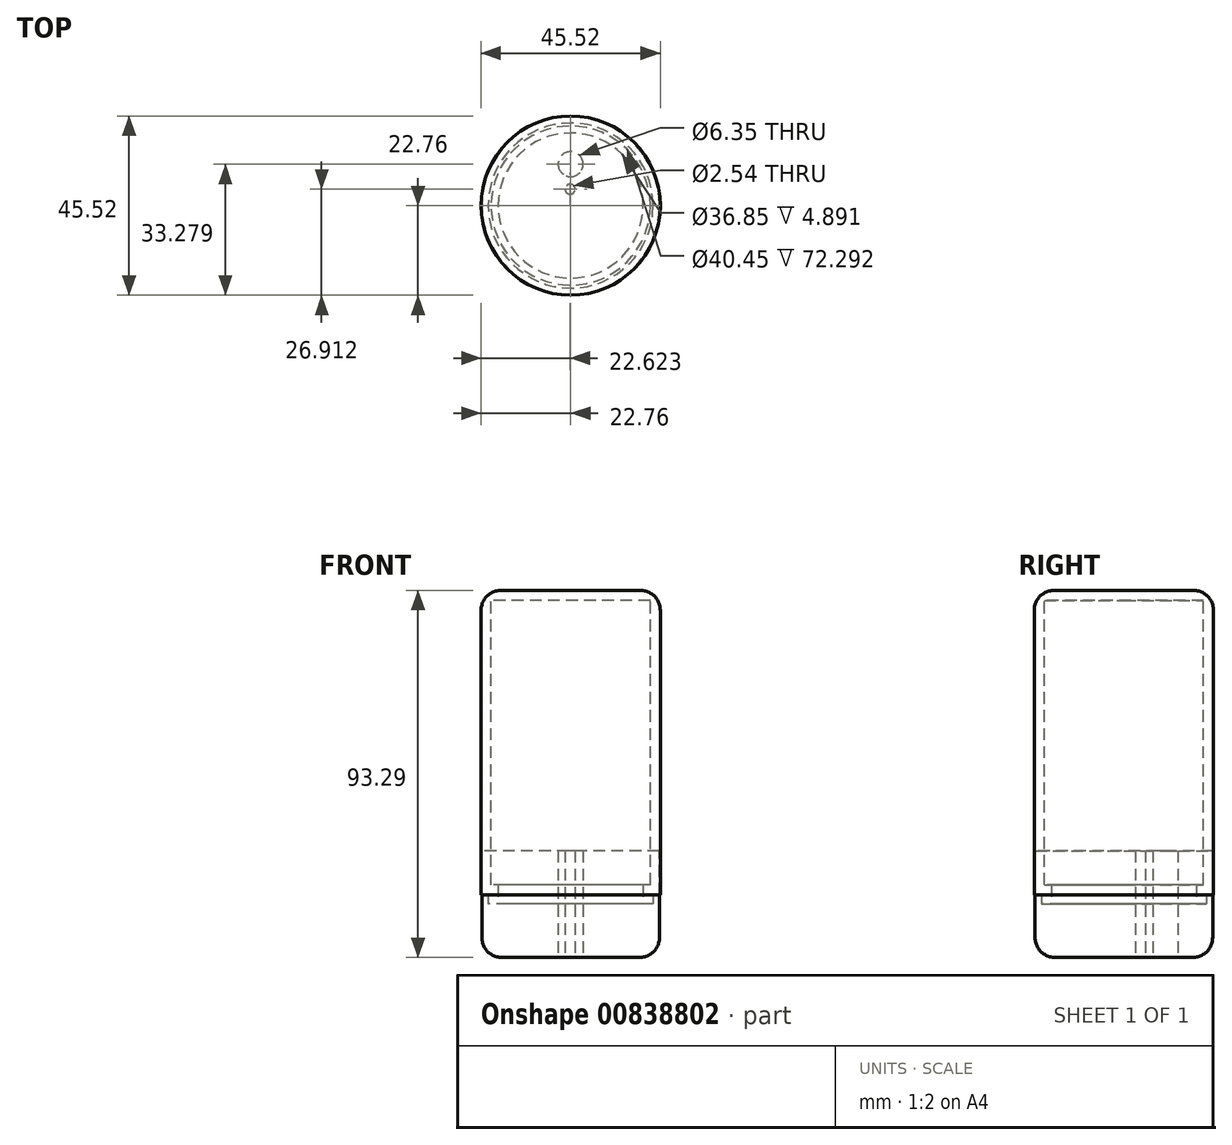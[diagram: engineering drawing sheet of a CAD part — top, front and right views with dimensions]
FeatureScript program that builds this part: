
annotation { "Feature Type Name" : "Feature", "Feature Type Description" : "" }
export const myFeature = defineFeature(function(context is Context, id is Id, definition is map)
    precondition{}
    {
        {
            var Q0;
            Q0=qCreatedBy(makeId("Top.planeOp"),FACE);
            var sketch = newSketch(context, id + "F0", { "sketchPlane" : qUnion([Q0])});
            skCircle(sketch, "E0", {"center": v(0, 0) * mm, "radius": 20.96 * mm});
            skSolve(sketch);
        }
        {
            var Q0;
            Q0=makeQuery(id+"F0.imprint","IMPRINT",FACE,{"disambiguationData":[TD([[makeQuery(id+"F0.imprint","IMPRINT",EDGE,{"derivedFrom":sQuery(id+"F0.wireOp",EDGE,"E0")}),1.0]])]});
            var Q1;
            Q1=sQuery(id+"F0.wireOp",EDGE,"E0");
            extrude(context, id + "F1", {"entities" : qUnion([Q0]), "surfaceEntities" : qUnion([Q1]), "depth" : 79.72 * mm, "offsetDistance" : 25.4 * mm});
        }
        {
            var Q0;
            Q0=makeQuery(id+"F1.opExtrude","CAP_FACE",FACE,{"disambiguationData":[OSD([sQuery(id+"F0.wireOp",EDGE,"E0")])],"isStart":false});
            var sketch = newSketch(context, id + "F2", { "sketchPlane" : qUnion([Q0])});
            skCircle(sketch, "E1", {"center": v(0, 0) * mm, "radius": 22.76 * mm});
            skSolve(sketch);
        }
        {
            var Q0;
            Q0=makeQuery(id+"F2.imprint","IMPRINT",FACE,{"disambiguationData":[TD([[makeQuery(id+"F2.imprint","IMPRINT",EDGE,{"derivedFrom":sQuery(id+"F2.wireOp",EDGE,"E1")}),1.0]])]});
            var Q1;
            Q1=sQuery(id+"F2.wireOp",EDGE,"E1");
            extrude(context, id + "F3", {"entities" : qUnion([Q0]), "operationType" : NewBodyOperationType.ADD, "surfaceEntities" : qUnion([Q1]), "oppositeDirection" : true, "depth" : 77.37 * mm, "offsetDistance" : 25.4 * mm});
        }
        {
            var Q0;
            Q0=makeQuery(id+"F1.opExtrude","CAP_FACE",FACE,{"disambiguationData":[OSD([sQuery(id+"F0.wireOp",EDGE,"E0")])],"isStart":true});
            shell(context, id + "F4", {"entities" : qUnion([Q0]), "thickness" : 2.54 * mm});
        }
        {
            var Q0;
            Q0=makeQuery(id+"F3.opExtrude","CAP_EDGE",EDGE,{"disambiguationData":[OSD([sQuery(id+"F2.wireOp",EDGE,"E1")])],"isStart":true});
            fillet(context, id + "F5", {"entities" : qUnion([Q0]), "radius" : 5.08 * mm, "tangentPropagation" : true, "allowEdgeOverflow" : false});
        }
        {
            var Q0;
            Q0=qCreatedBy(makeId("Top.planeOp"),FACE);
            var sketch = newSketch(context, id + "F6", { "sketchPlane" : qUnion([Q0])});
            skCircle(sketch, "E2", {"center": v(0, 0) * mm, "radius": 22.56 * mm});
            skSolve(sketch);
        }
        {
            var Q0;
            Q0=makeQuery(id+"F6.imprint","IMPRINT",FACE,{"disambiguationData":[TD([[makeQuery(id+"F6.imprint","IMPRINT",EDGE,{"derivedFrom":sQuery(id+"F6.wireOp",EDGE,"E2")}),1.0]])]});
            var Q1;
            Q1=sQuery(id+"F6.wireOp",EDGE,"E2");
            extrude(context, id + "F7", {"entities" : qUnion([Q0]), "surfaceEntities" : qUnion([Q1]), "endBound" : BoundingType.SYMMETRIC, "oppositeDirection" : true, "depth" : 27.14 * mm, "offsetDistance" : 25.4 * mm});
        }
        {
            var Q0;
            Q0=makeQuery(id+"F7.opExtrude","CAP_FACE",FACE,{"disambiguationData":[OSD([sQuery(id+"F6.wireOp",EDGE,"E2")])],"isStart":false});
            var sketch = newSketch(context, id + "F8", { "sketchPlane" : qUnion([Q0])});
            skPoint(sketch, "E3", {"position": v(0, -10.52) * mm});
            skSolve(sketch);
        }
        {
            var Q0;
            Q0=sQuery(id+"F8.wireOp",VERTEX,"E3");
            var Q1;
            Q1=makeQuery(id+"F7.opExtrude","SWEPT_BODY",BODY,{"disambiguationData":[OSD([sQuery(id+"F6.wireOp",EDGE,"E2")])]});
            hole(context, id + "F9", {"style" : HoleStyle.SIMPLE, "endStyle" : HoleEndStyle.BLIND, "holeDiameter" : 6.35 * mm, "majorDiameter" : 6.35 * mm, "holeDepth" : 31.75 * mm, "isTappedThrough" : true, "tappedDepth" : 12.7 * mm, "tapClearance" : 3, "locations" : qUnion([Q0]), "scope" : qUnion([Q1])});
        }
        {
            var Q0;
            Q0=makeQuery(id+"F7.opExtrude","CAP_EDGE",EDGE,{"disambiguationData":[OSD([sQuery(id+"F6.wireOp",EDGE,"E2")])],"isStart":false});
            fillet(context, id + "F10", {"entities" : qUnion([Q0]), "radius" : 5.08 * mm, "tangentPropagation" : true, "allowEdgeOverflow" : false});
        }
        {
            var Q0;
            Q0=makeQuery(id+"F7.opExtrude","CAP_FACE",FACE,{"disambiguationData":[OSD([sQuery(id+"F6.wireOp",EDGE,"E2")])],"isStart":false});
            var sketch = newSketch(context, id + "F11", { "sketchPlane" : qUnion([Q0])});
            skPoint(sketch, "E4", {"position": v(-0.14, -4.15) * mm});
            skSolve(sketch);
        }
        {
            var Q0;
            Q0=sQuery(id+"F11.wireOp",VERTEX,"E4");
            var Q1;
            Q1=makeQuery(id+"F7.opExtrude","SWEPT_BODY",BODY,{"disambiguationData":[OSD([sQuery(id+"F6.wireOp",EDGE,"E2")])]});
            hole(context, id + "F12", {"style" : HoleStyle.SIMPLE, "endStyle" : HoleEndStyle.BLIND, "holeDiameter" : 2.54 * mm, "majorDiameter" : 6.35 * mm, "holeDepth" : 31.75 * mm, "isTappedThrough" : true, "tappedDepth" : 12.7 * mm, "tapClearance" : 3, "locations" : qUnion([Q0]), "scope" : qUnion([Q1])});
        }
    });
